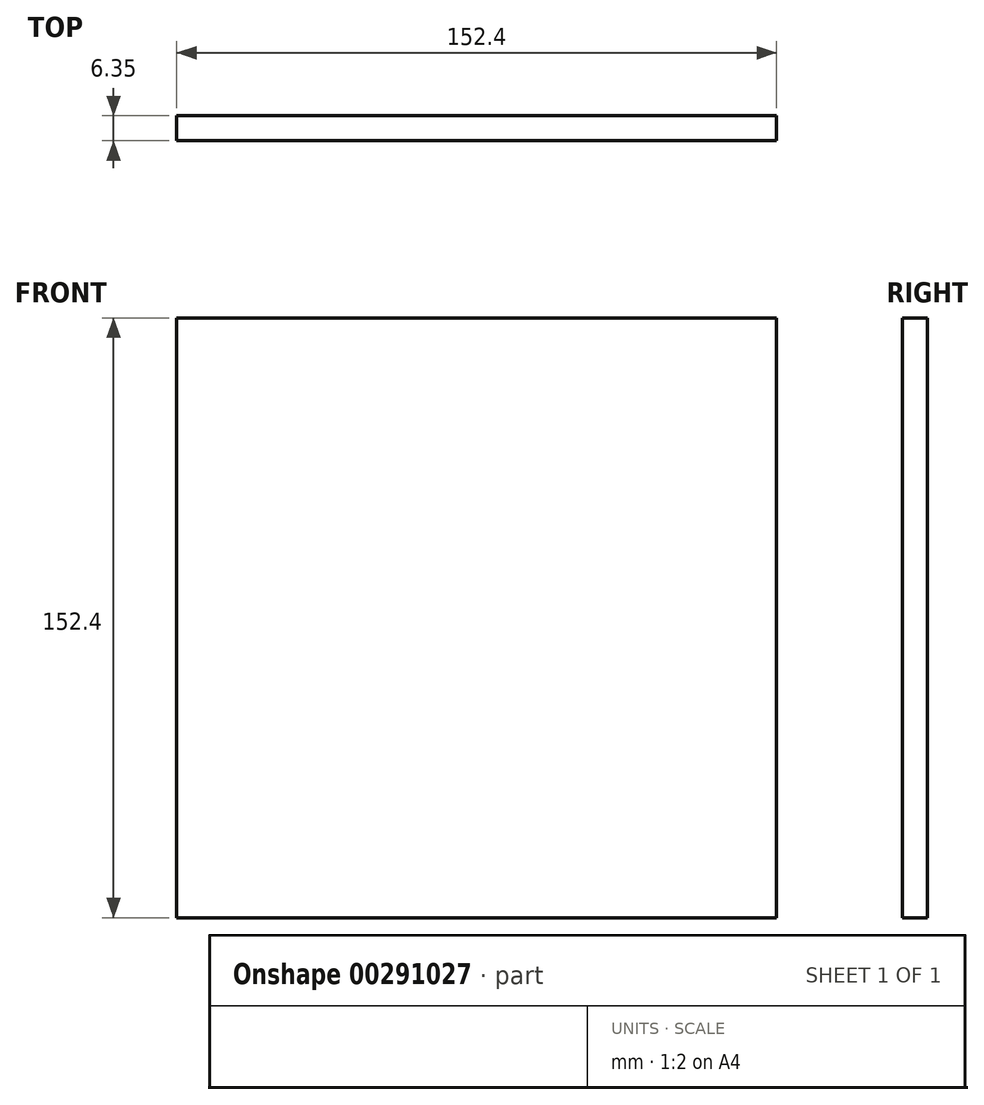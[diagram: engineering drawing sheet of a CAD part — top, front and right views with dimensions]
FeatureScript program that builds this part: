
annotation { "Feature Type Name" : "Feature", "Feature Type Description" : "" }
export const myFeature = defineFeature(function(context is Context, id is Id, definition is map)
    precondition{}
    {
        {
            var Q0;
            Q0=qCreatedBy(makeId("Front.planeOp"),FACE);
            var sketch = newSketch(context, id + "F0", { "sketchPlane" : qUnion([Q0])});
            skLineSegment(sketch, "E0.bottom", {"start": v(76.2, 76.2) * mm, "end": v(-76.2, 76.2) * mm});
            skLineSegment(sketch, "E0.top", {"start": v(76.2, -76.2) * mm, "end": v(-76.2, -76.2) * mm});
            skLineSegment(sketch, "E0.left", {"start": v(76.2, 76.2) * mm, "end": v(76.2, -76.2) * mm});
            skLineSegment(sketch, "E0.right", {"start": v(-76.2, 76.2) * mm, "end": v(-76.2, -76.2) * mm});
            skPoint(sketch, "E0.middle", {"position": v(0, 0) * mm});
            skSolve(sketch);
        }
        {
            var Q0;
            Q0=makeQuery(id+"F0.imprint","IMPRINT",FACE,{"disambiguationData":[TD([[makeQuery(id+"F0.imprint","IMPRINT",EDGE,{"derivedFrom":sQuery(id+"F0.wireOp",EDGE,"E0.bottom")}),1.0]])]});
            extrude(context, id + "F1", {"entities" : qUnion([Q0]), "depth" : 6.35 * mm});
        }
    });
